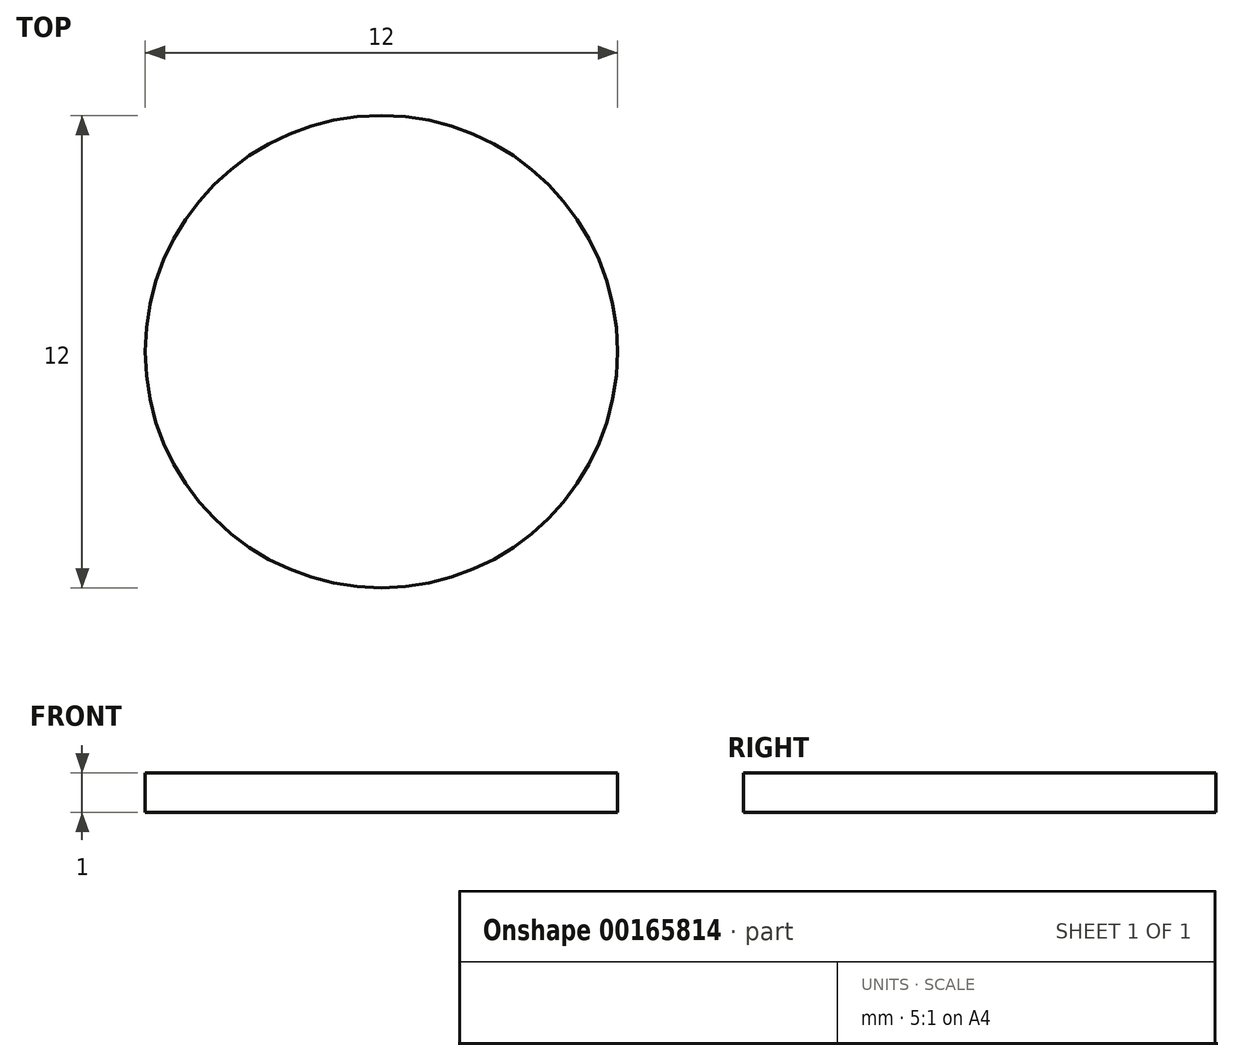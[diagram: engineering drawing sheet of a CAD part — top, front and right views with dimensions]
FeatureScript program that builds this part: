
annotation { "Feature Type Name" : "Feature", "Feature Type Description" : "" }
export const myFeature = defineFeature(function(context is Context, id is Id, definition is map)
    precondition{}
    {
        {
            var Q0;
            Q0=qCreatedBy(makeId("Top.planeOp"),FACE);
            var sketch = newSketch(context, id + "F0", { "sketchPlane" : qUnion([Q0])});
            skCircle(sketch, "E0", {"center": v(-29.4, 21.6) * mm, "radius": 6 * mm});
            skSolve(sketch);
        }
        {
            var Q0;
            Q0 = qSketchRegion(id + "F0", true);
            extrude(context, id + "F1", {"entities" : qUnion([Q0]), "depth" : 1 * mm});
        }
    });
